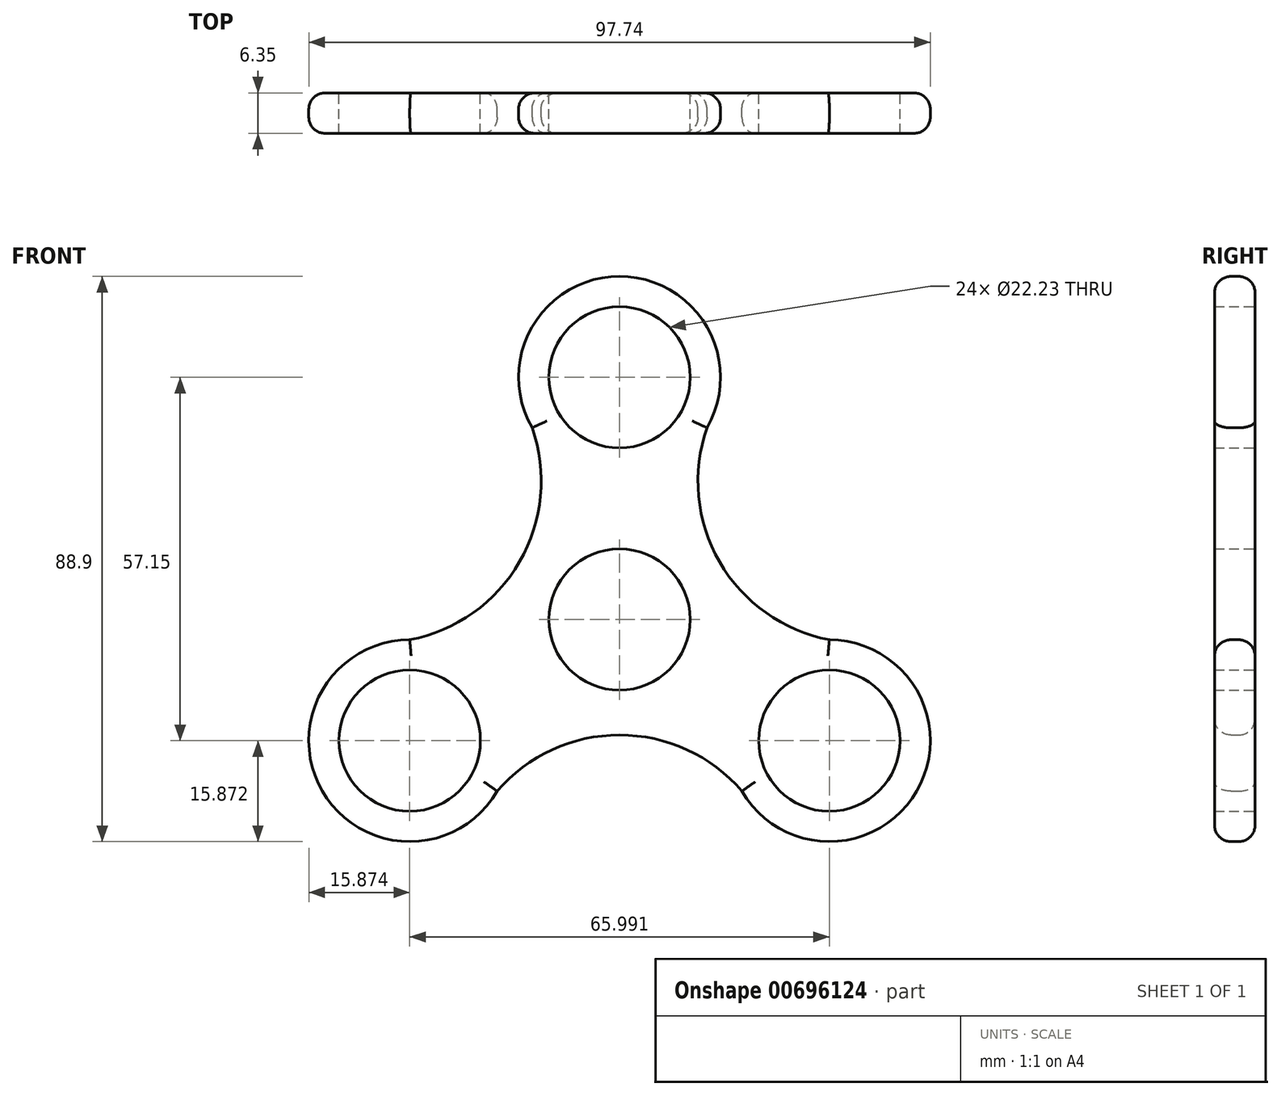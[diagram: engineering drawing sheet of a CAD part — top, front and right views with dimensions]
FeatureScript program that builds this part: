
annotation { "Feature Type Name" : "Feature", "Feature Type Description" : "" }
export const myFeature = defineFeature(function(context is Context, id is Id, definition is map)
    precondition{}
    {
        {
            var Q0;
            Q0=qCreatedBy(makeId("Front.planeOp"),FACE);
            var sketch = newSketch(context, id + "F0", { "sketchPlane" : qUnion([Q0])});
            skCircle(sketch, "E0", {"center": v(0, 52.26) * mm, "radius": 11.11 * mm});
            skCircle(sketch, "E1", {"center": v(0, 14.16) * mm, "radius": 11.11 * mm});
            skCircle(sketch, "E2", {"center": v(-33, -4.89) * mm, "radius": 11.11 * mm});
            skCircle(sketch, "E3", {"center": v(33, -4.89) * mm, "radius": 11.11 * mm});
            skArc(sketch, "E4", {"start": v(-33, 10.99) * mm, "mid": v(-46.74, -12.83) * mm, "end": v(-19.25, -12.83) * mm});
            skArc(sketch, "E5", {"start": v(13.75, 44.32) * mm, "mid": v(0, 68.14) * mm, "end": v(-13.75, 44.32) * mm});
            skArc(sketch, "E6", {"start": v(19.25, -12.83) * mm, "mid": v(46.74, -12.83) * mm, "end": v(33, 10.99) * mm});
            skArc(sketch, "E7", {"start": v(-33, 10.99) * mm, "mid": v(-15.73, 23.24) * mm, "end": v(-13.75, 44.32) * mm});
            skArc(sketch, "E8", {"start": v(13.75, 44.32) * mm, "mid": v(15.73, 23.24) * mm, "end": v(33, 10.99) * mm});
            skArc(sketch, "E9", {"start": v(19.25, -12.83) * mm, "mid": v(0, -4) * mm, "end": v(-19.25, -12.83) * mm});
            skSolve(sketch);
        }
        {
            var Q0;
            Q0=makeQuery(id+"F0.imprint","IMPRINT",FACE,{"disambiguationData":[TD([[makeQuery(id+"F0.imprint","IMPRINT",EDGE,{"derivedFrom":sQuery(id+"F0.wireOp",EDGE,"E0")}),-1.0]])]});
            extrude(context, id + "F1", {"entities" : qUnion([Q0]), "depth" : 6.35 * mm, "offsetDistance" : 25.4 * mm});
        }
        {
            var Q0;
            Q0=makeQuery(id+"F1.opExtrude","CAP_EDGE",EDGE,{"disambiguationData":[OSD([sQuery(id+"F0.wireOp",EDGE,"E4")])],"isStart":false});
            var Q1;
            Q1=makeQuery(id+"F1.opExtrude","CAP_EDGE",EDGE,{"disambiguationData":[OSD([sQuery(id+"F0.wireOp",EDGE,"E9")])],"isStart":false});
            var Q2;
            Q2=makeQuery(id+"F1.opExtrude","CAP_EDGE",EDGE,{"disambiguationData":[OSD([sQuery(id+"F0.wireOp",EDGE,"E6")])],"isStart":false});
            var Q3;
            Q3=makeQuery(id+"F1.opExtrude","CAP_EDGE",EDGE,{"disambiguationData":[OSD([sQuery(id+"F0.wireOp",EDGE,"E8")])],"isStart":false});
            var Q4;
            Q4=makeQuery(id+"F1.opExtrude","CAP_EDGE",EDGE,{"disambiguationData":[OSD([sQuery(id+"F0.wireOp",EDGE,"E5")])],"isStart":false});
            var Q5;
            Q5=makeQuery(id+"F1.opExtrude","CAP_EDGE",EDGE,{"disambiguationData":[OSD([sQuery(id+"F0.wireOp",EDGE,"E7")])],"isStart":false});
            var Q6;
            Q6=makeQuery(id+"F1.opExtrude","CAP_EDGE",EDGE,{"disambiguationData":[OSD([sQuery(id+"F0.wireOp",EDGE,"E9")])],"isStart":true});
            var Q7;
            Q7=makeQuery(id+"F1.opExtrude","CAP_EDGE",EDGE,{"disambiguationData":[OSD([sQuery(id+"F0.wireOp",EDGE,"E6")])],"isStart":true});
            var Q8;
            Q8=makeQuery(id+"F1.opExtrude","CAP_EDGE",EDGE,{"disambiguationData":[OSD([sQuery(id+"F0.wireOp",EDGE,"E8")])],"isStart":true});
            var Q9;
            Q9=makeQuery(id+"F1.opExtrude","CAP_EDGE",EDGE,{"disambiguationData":[OSD([sQuery(id+"F0.wireOp",EDGE,"E5")])],"isStart":true});
            var Q10;
            Q10=makeQuery(id+"F1.opExtrude","CAP_EDGE",EDGE,{"disambiguationData":[OSD([sQuery(id+"F0.wireOp",EDGE,"E7")])],"isStart":true});
            var Q11;
            Q11=makeQuery(id+"F1.opExtrude","CAP_EDGE",EDGE,{"disambiguationData":[OSD([sQuery(id+"F0.wireOp",EDGE,"E4")])],"isStart":true});
            fillet(context, id + "F2", {"entities" : qUnion([Q0, Q1, Q2, Q3, Q4, Q5, Q6, Q7, Q8, Q9, Q10, Q11]), "radius" : 2.54 * mm, "tangentPropagation" : true, "allowEdgeOverflow" : false});
        }
    });
